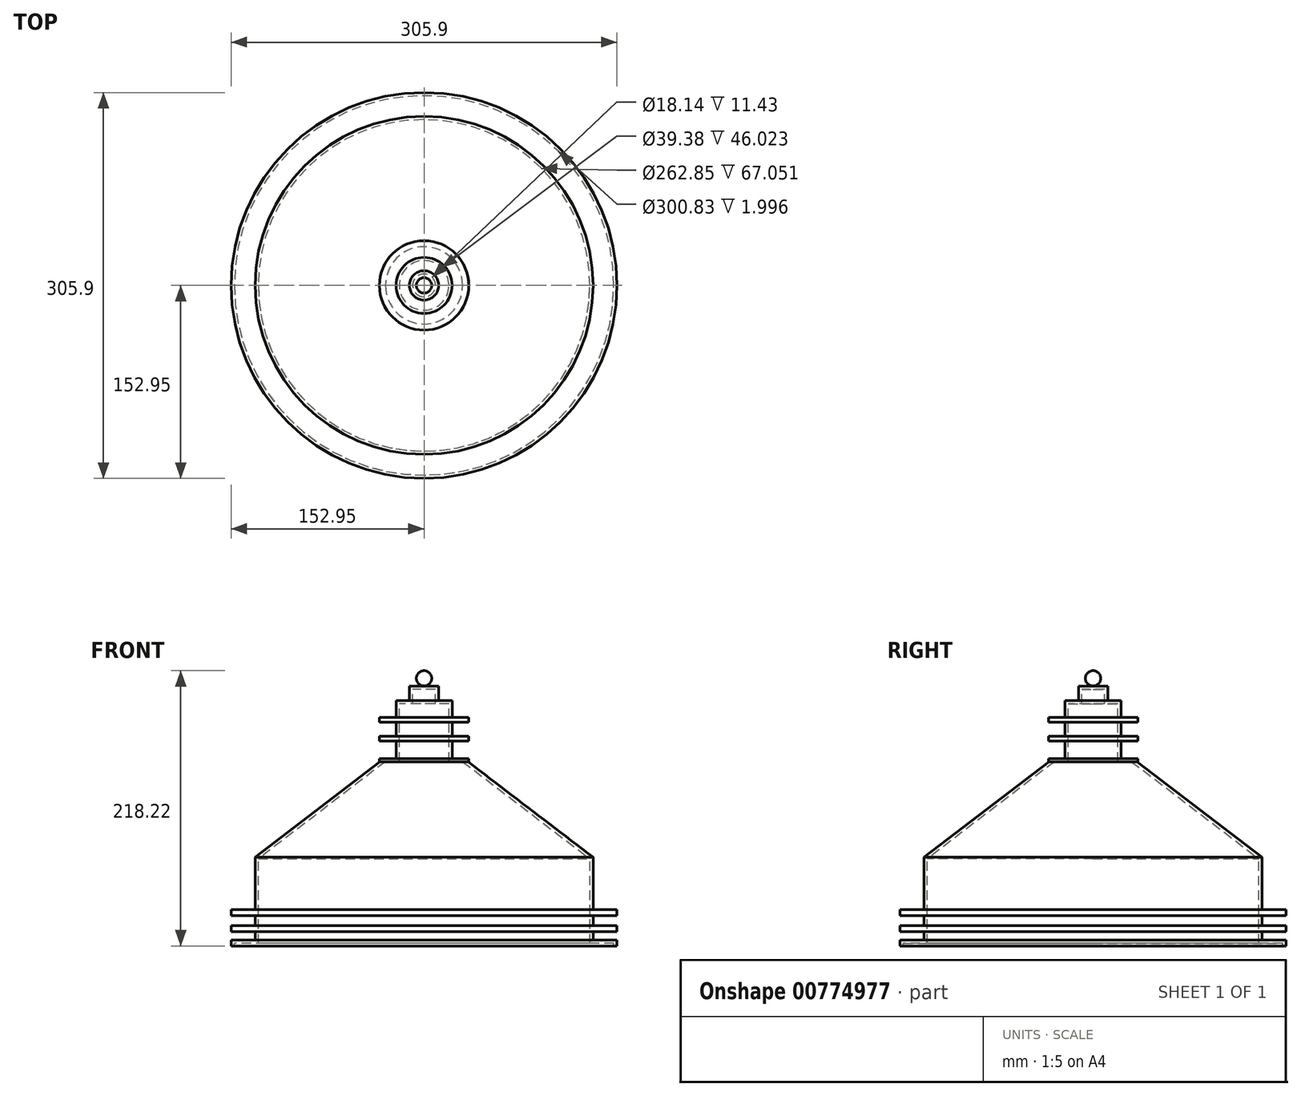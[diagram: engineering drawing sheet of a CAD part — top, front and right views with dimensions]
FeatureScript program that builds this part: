
annotation { "Feature Type Name" : "Feature", "Feature Type Description" : "" }
export const myFeature = defineFeature(function(context is Context, id is Id, definition is map)
    precondition{}
    {
        {
            var Q0;
            Q0=qCreatedBy(makeId("Front.planeOp"),FACE);
            var sketch = newSketch(context, id + "F0", { "sketchPlane" : qUnion([Q0])});
            skArc(sketch, "E0", {"start": v(0, 30.39) * mm, "mid": v(-6.08, 24.31) * mm, "end": v(0, 18.23) * mm});
            skLineSegment(sketch, "E1", {"start": v(0, 18.23) * mm, "end": v(-11.61, 18.23) * mm});
            skLineSegment(sketch, "E2", {"start": v(-11.61, 18.23) * mm, "end": v(-11.61, 6.8) * mm});
            skLineSegment(sketch, "E3", {"start": v(0, 6.8) * mm, "end": v(-22.23, 6.8) * mm});
            skLineSegment(sketch, "E4", {"start": v(-22.23, 6.8) * mm, "end": v(-22.23, -6.56) * mm});
            skLineSegment(sketch, "E5", {"start": v(0, -6.56) * mm, "end": v(-35.43, -6.56) * mm});
            skLineSegment(sketch, "E6", {"start": v(-35.43, -6.56) * mm, "end": v(-35.43, -10.42) * mm});
            skLineSegment(sketch, "E7", {"start": v(-35.43, -10.42) * mm, "end": v(0, -10.42) * mm});
            skLineSegment(sketch, "E8", {"start": v(-22.23, -10.42) * mm, "end": v(-22.23, -21.54) * mm});
            skLineSegment(sketch, "E9", {"start": v(0, -21.54) * mm, "end": v(-35.43, -21.54) * mm});
            skLineSegment(sketch, "E10", {"start": v(-35.43, -21.54) * mm, "end": v(-35.43, -25.25) * mm});
            skLineSegment(sketch, "E11", {"start": v(-35.43, -25.25) * mm, "end": v(0, -25.25) * mm});
            skLineSegment(sketch, "E12", {"start": v(-22.23, -25.25) * mm, "end": v(-22.23, -39.22) * mm});
            skLineSegment(sketch, "E13", {"start": v(0, -41.94) * mm, "end": v(-35.43, -41.94) * mm});
            skPoint(sketch, "E14.end.orphan", {"position": v(0, -39.22) * mm});
            skLineSegment(sketch, "E15", {"start": v(0, -39.22) * mm, "end": v(-35.43, -39.22) * mm});
            skLineSegment(sketch, "E16", {"start": v(-35.43, -39.22) * mm, "end": v(-35.43, -41.94) * mm});
            skLineSegment(sketch, "E17", {"start": v(-35.03, -41.94) * mm, "end": v(-133.97, -117.53) * mm});
            skLineSegment(sketch, "E18", {"start": v(-133.97, -117.53) * mm, "end": v(-133.97, -159.16) * mm});
            skLineSegment(sketch, "E19", {"start": v(-133.97, -159.16) * mm, "end": v(-152.95, -159.16) * mm});
            skLineSegment(sketch, "E20", {"start": v(-152.95, -159.16) * mm, "end": v(-152.95, -163.7) * mm});
            skLineSegment(sketch, "E21", {"start": v(-152.95, -163.7) * mm, "end": v(-133.97, -163.7) * mm});
            skLineSegment(sketch, "E22", {"start": v(-133.97, -163.7) * mm, "end": v(-133.97, -171.68) * mm});
            skLineSegment(sketch, "E23", {"start": v(-133.97, -171.68) * mm, "end": v(-152.95, -171.68) * mm});
            skLineSegment(sketch, "E24", {"start": v(-152.95, -171.68) * mm, "end": v(-152.95, -176.58) * mm});
            skLineSegment(sketch, "E25", {"start": v(-152.95, -176.58) * mm, "end": v(-133.97, -176.58) * mm});
            skLineSegment(sketch, "E26", {"start": v(-133.97, -176.58) * mm, "end": v(-133.97, -183.3) * mm});
            skLineSegment(sketch, "E27", {"start": v(-133.97, -183.3) * mm, "end": v(-152.95, -183.3) * mm});
            skLineSegment(sketch, "E28", {"start": v(-152.95, -183.3) * mm, "end": v(-152.95, -187.83) * mm});
            skPoint(sketch, "E29.end.orphan", {"position": v(0, -187.83) * mm});
            skLineSegment(sketch, "E30", {"start": v(-152.95, -187.83) * mm, "end": v(0, -187.83) * mm});
            skLineSegment(sketch, "E31", {"start": v(0, 30.39) * mm, "end": v(0, -187.83) * mm});
            skSolve(sketch);
        }
        {
            var Q0;
            {var subQ3=sQuery(id+"F0.wireOp",EDGE,"E17");Q0=makeQuery(id+"F0.imprint","IMPRINT",FACE,{"disambiguationData":[TD([[makeQuery(id+"F0.imprint","IMPRINT",EDGE,{"derivedFrom":subQ3}),1.0]])]});}
            var Q1;
            {var subQ0=sQuery(id+"F0.wireOp",EDGE,"E0");Q1=makeQuery(id+"F0.imprint","IMPRINT",FACE,{"disambiguationData":[TD([[makeQuery(id+"F0.imprint","IMPRINT",EDGE,{"derivedFrom":subQ0}),1.0]])]});}
            var Q2;
            {var subQ0=sQuery(id+"F0.wireOp",EDGE,"E1");Q2=makeQuery(id+"F0.imprint","IMPRINT",FACE,{"disambiguationData":[TD([[makeQuery(id+"F0.imprint","IMPRINT",EDGE,{"derivedFrom":subQ0}),1.0]])]});}
            var Q3;
            {var subQ1=sQuery(id+"F0.wireOp",EDGE,"E4");Q3=makeQuery(id+"F0.imprint","IMPRINT",FACE,{"disambiguationData":[TD([[makeQuery(id+"F0.imprint","IMPRINT",EDGE,{"derivedFrom":subQ1}),1.0]])]});}
            var Q4;
            {var subQ1=sQuery(id+"F0.wireOp",EDGE,"E6");Q4=makeQuery(id+"F0.imprint","IMPRINT",FACE,{"disambiguationData":[TD([[makeQuery(id+"F0.imprint","IMPRINT",EDGE,{"derivedFrom":subQ1}),1.0]])]});}
            var Q5;
            {var subQ3=sQuery(id+"F0.wireOp",EDGE,"E8");Q5=makeQuery(id+"F0.imprint","IMPRINT",FACE,{"disambiguationData":[TD([[makeQuery(id+"F0.imprint","IMPRINT",EDGE,{"derivedFrom":subQ3}),1.0]])]});}
            var Q6;
            {var subQ1=sQuery(id+"F0.wireOp",EDGE,"E10");Q6=makeQuery(id+"F0.imprint","IMPRINT",FACE,{"disambiguationData":[TD([[makeQuery(id+"F0.imprint","IMPRINT",EDGE,{"derivedFrom":subQ1}),1.0]])]});}
            var Q7;
            {var subQ3=sQuery(id+"F0.wireOp",EDGE,"E12");Q7=makeQuery(id+"F0.imprint","IMPRINT",FACE,{"disambiguationData":[TD([[makeQuery(id+"F0.imprint","IMPRINT",EDGE,{"derivedFrom":subQ3}),1.0]])]});}
            var Q8;
            {var subQ2=sQuery(id+"F0.wireOp",EDGE,"E16");Q8=makeQuery(id+"F0.imprint","IMPRINT",FACE,{"disambiguationData":[TD([[makeQuery(id+"F0.imprint","IMPRINT",EDGE,{"derivedFrom":subQ2}),1.0]])]});}
            var Q9;
            Q9=sQuery(id+"F0.wireOp",EDGE,"E31");
            revolve(context, id + "F1", {"surfaceOperationType" : NewSurfaceOperationType.NEW, "entities" : qUnion([Q0, Q1, Q2, Q3, Q4, Q5, Q6, Q7, Q8]), "axis" : qUnion([Q9]), "revolveType" : RevolveType.FULL});
        }
        {
            var Q0;
            Q0=makeQuery(id+"F1.opRevolve","SWEPT_FACE",FACE,{"disambiguationData":[OSD([sQuery(id+"F0.wireOp",EDGE,"E30")])]});
            shell(context, id + "F2", {"entities" : qUnion([Q0]), "thickness" : 2.54 * mm});
        }
    });
